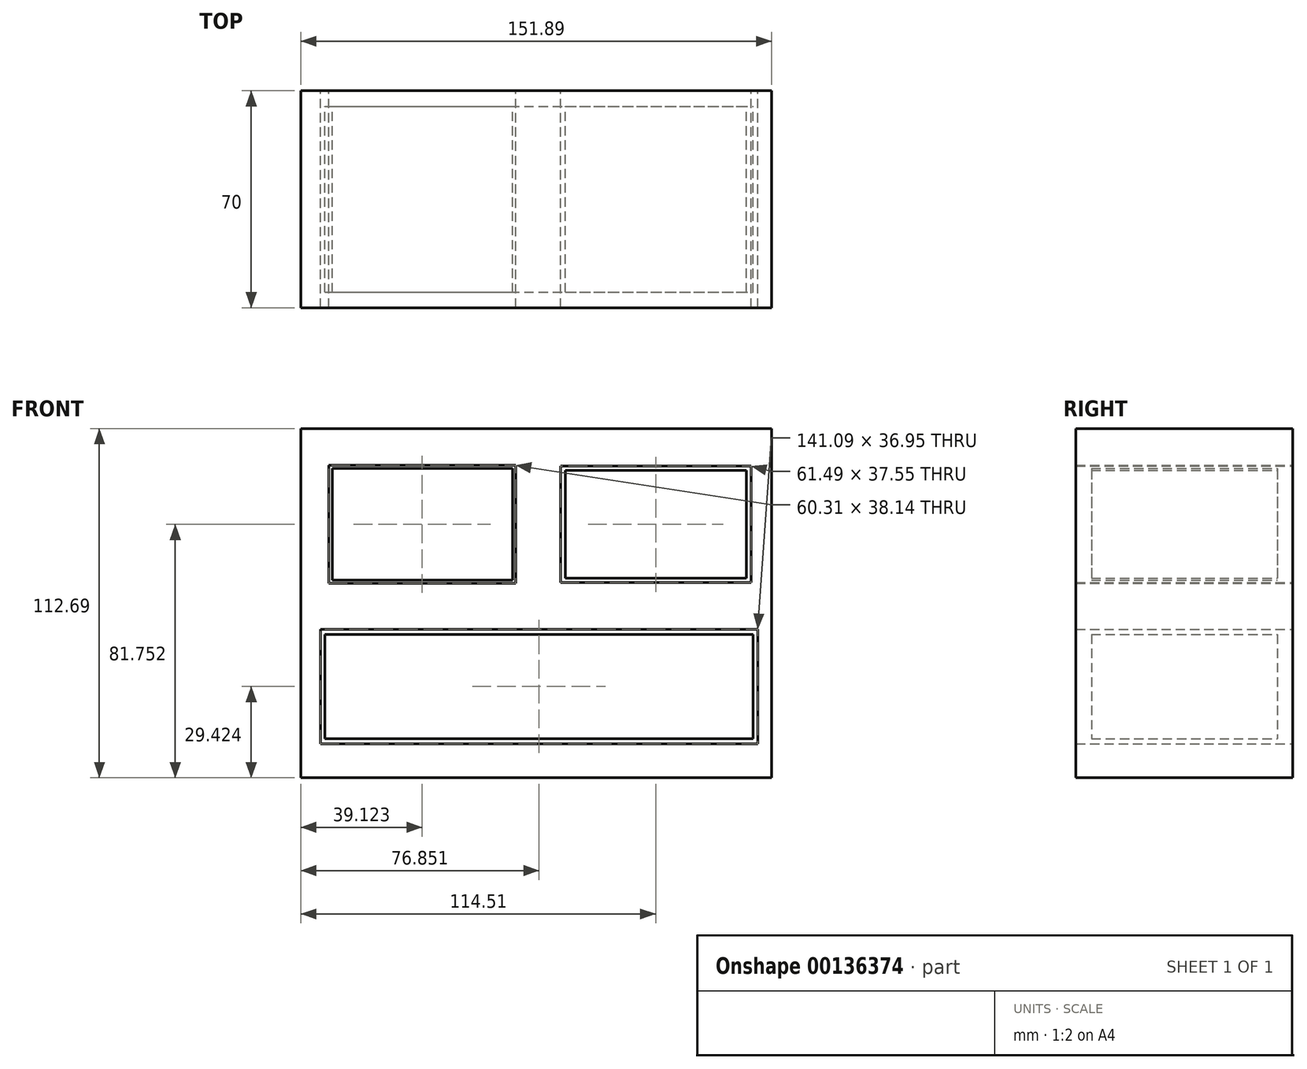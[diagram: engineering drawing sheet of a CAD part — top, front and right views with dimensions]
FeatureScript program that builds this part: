
annotation { "Feature Type Name" : "Feature", "Feature Type Description" : "" }
export const myFeature = defineFeature(function(context is Context, id is Id, definition is map)
    precondition{}
    {
        {
            var Q0;
            Q0=qCreatedBy(makeId("Front.planeOp"),FACE);
            var sketch = newSketch(context, id + "F0", { "sketchPlane" : qUnion([Q0])});
            skLineSegment(sketch, "E0.bottom", {"start": v(-75.22, 56.2) * mm, "end": v(76.67, 56.2) * mm});
            skLineSegment(sketch, "E0.top", {"start": v(-75.22, -56.49) * mm, "end": v(76.67, -56.49) * mm});
            skLineSegment(sketch, "E0.left", {"start": v(-75.22, 56.2) * mm, "end": v(-75.22, -56.49) * mm});
            skLineSegment(sketch, "E0.right", {"start": v(76.67, 56.2) * mm, "end": v(76.67, -56.49) * mm});
            skLineSegment(sketch, "E1.bottom", {"start": v(-66.25, 44.33) * mm, "end": v(-5.94, 44.33) * mm});
            skLineSegment(sketch, "E1.top", {"start": v(-66.25, 6.2) * mm, "end": v(-5.94, 6.2) * mm});
            skLineSegment(sketch, "E1.left", {"start": v(-66.25, 44.33) * mm, "end": v(-66.25, 6.2) * mm});
            skLineSegment(sketch, "E1.right", {"start": v(-5.94, 44.33) * mm, "end": v(-5.94, 6.2) * mm});
            skLineSegment(sketch, "E2.bottom", {"start": v(8.54, 44.03) * mm, "end": v(70.04, 44.03) * mm});
            skLineSegment(sketch, "E2.top", {"start": v(8.54, 6.49) * mm, "end": v(70.04, 6.49) * mm});
            skLineSegment(sketch, "E2.left", {"start": v(8.54, 44.03) * mm, "end": v(8.54, 6.49) * mm});
            skLineSegment(sketch, "E2.right", {"start": v(70.04, 44.03) * mm, "end": v(70.04, 6.49) * mm});
            skLineSegment(sketch, "E3.bottom", {"start": v(-68.91, -8.59) * mm, "end": v(72.18, -8.59) * mm});
            skLineSegment(sketch, "E3.top", {"start": v(-68.91, -45.54) * mm, "end": v(72.18, -45.54) * mm});
            skLineSegment(sketch, "E3.left", {"start": v(-68.91, -8.59) * mm, "end": v(-68.91, -45.54) * mm});
            skLineSegment(sketch, "E3.right", {"start": v(72.18, -8.59) * mm, "end": v(72.18, -45.54) * mm});
            skSolve(sketch);
        }
        {
            var Q0;
            Q0=makeQuery(id+"F0.imprint","IMPRINT",FACE,{"disambiguationData":[TD([[makeQuery(id+"F0.imprint","IMPRINT",EDGE,{"derivedFrom":sQuery(id+"F0.wireOp",EDGE,"E0.bottom")}),-1.0]])]});
            extrude(context, id + "F1", {"entities" : qUnion([Q0]), "endBound" : BoundingType.SYMMETRIC, "depth" : 70 * mm});
        }
        {
            var Q0;
            Q0=qCreatedBy(makeId("Front.planeOp"),FACE);
            var sketch = newSketch(context, id + "F2", { "sketchPlane" : qUnion([Q0])});
            skLineSegment(sketch, "E4.bottom", {"start": v(-65.08, 43.34) * mm, "end": v(-6.89, 43.34) * mm});
            skLineSegment(sketch, "E4.top", {"start": v(-65.08, 7.27) * mm, "end": v(-6.89, 7.27) * mm});
            skLineSegment(sketch, "E4.left", {"start": v(-65.08, 43.34) * mm, "end": v(-65.08, 7.27) * mm});
            skLineSegment(sketch, "E4.right", {"start": v(-6.89, 43.34) * mm, "end": v(-6.89, 7.27) * mm});
            skLineSegment(sketch, "E5.bottom", {"start": v(10.08, 42.73) * mm, "end": v(68.58, 42.73) * mm});
            skLineSegment(sketch, "E5.top", {"start": v(10.08, 7.88) * mm, "end": v(68.58, 7.88) * mm});
            skLineSegment(sketch, "E5.left", {"start": v(10.08, 42.73) * mm, "end": v(10.08, 7.88) * mm});
            skLineSegment(sketch, "E5.right", {"start": v(68.58, 42.73) * mm, "end": v(68.58, 7.88) * mm});
            skLineSegment(sketch, "E6.bottom", {"start": v(-67.5, -10.3) * mm, "end": v(70.7, -10.3) * mm});
            skLineSegment(sketch, "E6.top", {"start": v(-67.5, -43.94) * mm, "end": v(70.7, -43.94) * mm});
            skLineSegment(sketch, "E6.left", {"start": v(-67.5, -10.3) * mm, "end": v(-67.5, -43.94) * mm});
            skLineSegment(sketch, "E6.right", {"start": v(70.7, -10.3) * mm, "end": v(70.7, -43.94) * mm});
            skSolve(sketch);
        }
        {
            var Q0;
            Q0=makeQuery(id+"F2.imprint","IMPRINT",FACE,{"disambiguationData":[TD([[makeQuery(id+"F2.imprint","IMPRINT",EDGE,{"derivedFrom":sQuery(id+"F2.wireOp",EDGE,"E6.bottom")}),-1.0]])]});
            var Q1;
            Q1=makeQuery(id+"F2.imprint","IMPRINT",FACE,{"disambiguationData":[TD([[makeQuery(id+"F2.imprint","IMPRINT",EDGE,{"derivedFrom":sQuery(id+"F2.wireOp",EDGE,"E4.bottom")}),-1.0]])]});
            var Q2;
            Q2=makeQuery(id+"F2.imprint","IMPRINT",FACE,{"disambiguationData":[TD([[makeQuery(id+"F2.imprint","IMPRINT",EDGE,{"derivedFrom":sQuery(id+"F2.wireOp",EDGE,"E5.bottom")}),-1.0]])]});
            extrude(context, id + "F3", {"entities" : qUnion([Q0, Q1, Q2]), "endBound" : BoundingType.SYMMETRIC, "depth" : 60 * mm});
        }
    });
